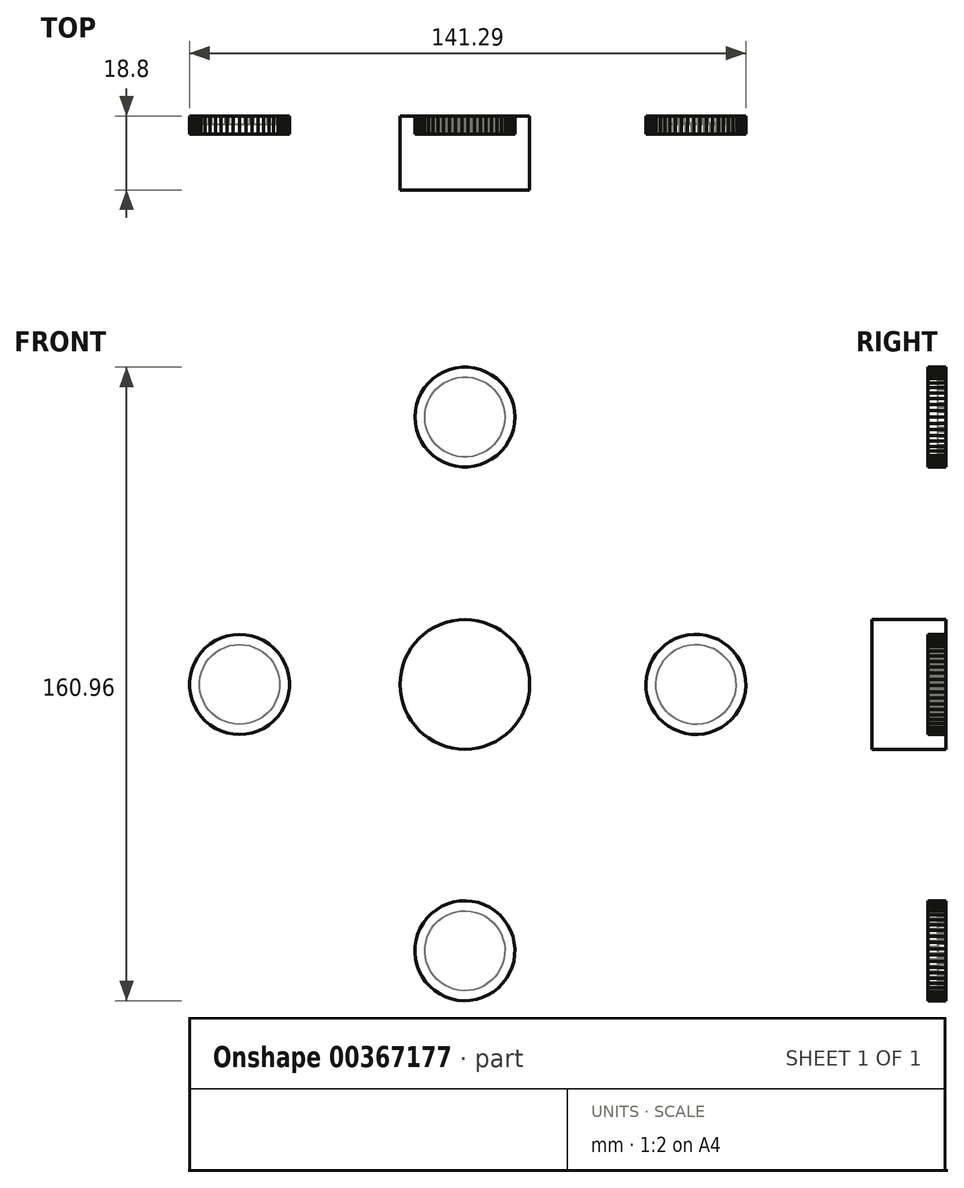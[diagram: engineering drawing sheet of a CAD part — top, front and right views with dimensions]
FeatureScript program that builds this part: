
annotation { "Feature Type Name" : "Feature", "Feature Type Description" : "" }
export const myFeature = defineFeature(function(context is Context, id is Id, definition is map)
    precondition{}
    {
        {
            var Q0;
            Q0=qCreatedBy(makeId("Front.planeOp"),FACE);
            var sketch = newSketch(context, id + "F0", { "sketchPlane" : qUnion([Q0])});
            skCircle(sketch, "E0", {"center": v(0, 0) * mm, "radius": 16.46 * mm});
            skSolve(sketch);
        }
        {
            var Q0;
            Q0=makeQuery(id+"F0.imprint","IMPRINT",FACE,{"disambiguationData":[TD([[makeQuery(id+"F0.imprint","IMPRINT",EDGE,{"derivedFrom":sQuery(id+"F0.wireOp",EDGE,"E0")}),1.0]])]});
            extrude(context, id + "F1", {"entities" : qUnion([Q0]), "depth" : 18.8 * mm});
        }
        {
            var Q0;
            Q0=qCreatedBy(makeId("Top.planeOp"),FACE);
            var sketch = newSketch(context, id + "F2", { "sketchPlane" : qUnion([Q0])});
            skCircle(sketch, "E1", {"center": v(0, -9.63) * mm, "radius": 6.4 * mm});
            skSolve(sketch);
        }
        {
            var Q0;
            Q0=sQuery(id+"F2.wireOp",EDGE,"E1");
            extrude(context, id + "F3", {"bodyType" : ToolBodyType.SURFACE, "surfaceEntities" : qUnion([Q0]), "endBound" : BoundingType.SYMMETRIC, "depth" : 134.62 * mm});
        }
        {
            var Q0;
            Q0=qCreatedBy(makeId("Right.planeOp"),FACE);
            var sketch = newSketch(context, id + "F4", { "sketchPlane" : qUnion([Q0])});
            skCircle(sketch, "E2", {"center": v(-9.55, 0) * mm, "radius": 4.67 * mm});
            skSolve(sketch);
        }
        {
            var Q0;
            Q0=sQuery(id+"F4.wireOp",EDGE,"E2");
            extrude(context, id + "F5", {"bodyType" : ToolBodyType.SURFACE, "surfaceEntities" : qUnion([Q0]), "endBound" : BoundingType.SYMMETRIC, "depth" : 115.82 * mm});
        }
        {
            var Q0;
            Q0=qCreatedBy(makeId("Front.planeOp"),FACE);
            var sketch = newSketch(context, id + "F6", { "sketchPlane" : qUnion([Q0])});
            skCircle(sketch, "E3.cCircle", {"center": v(0, 67.94) * mm, "radius": 12.67 * mm, "construction": true});
            skLineSegment(sketch, "E3.0", {"start": v(-0.8, 80.61) * mm, "end": v(0.8, 80.61) * mm});
            skLineSegment(sketch, "E3.1", {"start": v(0.8, 80.61) * mm, "end": v(2.38, 80.41) * mm});
            skLineSegment(sketch, "E3.2", {"start": v(2.38, 80.41) * mm, "end": v(3.92, 80.02) * mm});
            skLineSegment(sketch, "E3.3", {"start": v(3.92, 80.02) * mm, "end": v(5.4, 79.43) * mm});
            skLineSegment(sketch, "E3.4", {"start": v(5.4, 79.43) * mm, "end": v(6.8, 78.66) * mm});
            skLineSegment(sketch, "E3.5", {"start": v(6.8, 78.66) * mm, "end": v(8.1, 77.72) * mm});
            skLineSegment(sketch, "E3.6", {"start": v(8.1, 77.72) * mm, "end": v(9.26, 76.63) * mm});
            skLineSegment(sketch, "E3.7", {"start": v(9.26, 76.63) * mm, "end": v(10.27, 75.4) * mm});
            skLineSegment(sketch, "E3.8", {"start": v(10.27, 75.4) * mm, "end": v(11.13, 74.06) * mm});
            skLineSegment(sketch, "E3.9", {"start": v(11.13, 74.06) * mm, "end": v(11.8, 72.61) * mm});
            skLineSegment(sketch, "E3.10", {"start": v(11.8, 72.61) * mm, "end": v(12.3, 71.1) * mm});
            skLineSegment(sketch, "E3.11", {"start": v(12.3, 71.1) * mm, "end": v(12.6, 69.53) * mm});
            skLineSegment(sketch, "E3.12", {"start": v(12.6, 69.53) * mm, "end": v(12.7, 67.94) * mm});
            skLineSegment(sketch, "E3.13", {"start": v(12.7, 67.94) * mm, "end": v(12.6, 66.35) * mm});
            skLineSegment(sketch, "E3.14", {"start": v(12.6, 66.35) * mm, "end": v(12.3, 64.78) * mm});
            skLineSegment(sketch, "E3.15", {"start": v(12.3, 64.78) * mm, "end": v(11.8, 63.26) * mm});
            skLineSegment(sketch, "E3.16", {"start": v(11.8, 63.26) * mm, "end": v(11.13, 61.82) * mm});
            skLineSegment(sketch, "E3.17", {"start": v(11.13, 61.82) * mm, "end": v(10.27, 60.47) * mm});
            skLineSegment(sketch, "E3.18", {"start": v(10.27, 60.47) * mm, "end": v(9.26, 59.24) * mm});
            skLineSegment(sketch, "E3.19", {"start": v(9.26, 59.24) * mm, "end": v(8.1, 58.15) * mm});
            skLineSegment(sketch, "E3.20", {"start": v(8.1, 58.15) * mm, "end": v(6.8, 57.22) * mm});
            skLineSegment(sketch, "E3.21", {"start": v(6.8, 57.22) * mm, "end": v(5.4, 56.45) * mm});
            skLineSegment(sketch, "E3.22", {"start": v(5.4, 56.45) * mm, "end": v(3.92, 55.86) * mm});
            skLineSegment(sketch, "E3.23", {"start": v(3.92, 55.86) * mm, "end": v(2.38, 55.46) * mm});
            skLineSegment(sketch, "E3.24", {"start": v(2.38, 55.46) * mm, "end": v(0.8, 55.26) * mm});
            skLineSegment(sketch, "E3.25", {"start": v(0.8, 55.26) * mm, "end": v(-0.8, 55.26) * mm});
            skLineSegment(sketch, "E3.26", {"start": v(-0.8, 55.26) * mm, "end": v(-2.38, 55.46) * mm});
            skLineSegment(sketch, "E3.27", {"start": v(-2.38, 55.46) * mm, "end": v(-3.92, 55.86) * mm});
            skLineSegment(sketch, "E3.28", {"start": v(-3.92, 55.86) * mm, "end": v(-5.4, 56.45) * mm});
            skLineSegment(sketch, "E3.29", {"start": v(-5.4, 56.45) * mm, "end": v(-6.8, 57.22) * mm});
            skLineSegment(sketch, "E3.30", {"start": v(-6.8, 57.22) * mm, "end": v(-8.1, 58.15) * mm});
            skLineSegment(sketch, "E3.31", {"start": v(-8.1, 58.15) * mm, "end": v(-9.26, 59.24) * mm});
            skLineSegment(sketch, "E3.32", {"start": v(-9.26, 59.24) * mm, "end": v(-10.27, 60.47) * mm});
            skLineSegment(sketch, "E3.33", {"start": v(-10.27, 60.47) * mm, "end": v(-11.13, 61.82) * mm});
            skLineSegment(sketch, "E3.34", {"start": v(-11.13, 61.82) * mm, "end": v(-11.8, 63.26) * mm});
            skLineSegment(sketch, "E3.35", {"start": v(-11.8, 63.26) * mm, "end": v(-12.3, 64.78) * mm});
            skLineSegment(sketch, "E3.36", {"start": v(-12.3, 64.78) * mm, "end": v(-12.6, 66.35) * mm});
            skLineSegment(sketch, "E3.37", {"start": v(-12.6, 66.35) * mm, "end": v(-12.7, 67.94) * mm});
            skLineSegment(sketch, "E3.38", {"start": v(-12.7, 67.94) * mm, "end": v(-12.6, 69.53) * mm});
            skLineSegment(sketch, "E3.39", {"start": v(-12.6, 69.53) * mm, "end": v(-12.3, 71.1) * mm});
            skLineSegment(sketch, "E3.40", {"start": v(-12.3, 71.1) * mm, "end": v(-11.8, 72.61) * mm});
            skLineSegment(sketch, "E3.41", {"start": v(-11.8, 72.61) * mm, "end": v(-11.13, 74.06) * mm});
            skLineSegment(sketch, "E3.42", {"start": v(-11.13, 74.06) * mm, "end": v(-10.27, 75.4) * mm});
            skLineSegment(sketch, "E3.43", {"start": v(-10.27, 75.4) * mm, "end": v(-9.26, 76.63) * mm});
            skLineSegment(sketch, "E3.44", {"start": v(-9.26, 76.63) * mm, "end": v(-8.1, 77.72) * mm});
            skLineSegment(sketch, "E3.45", {"start": v(-8.1, 77.72) * mm, "end": v(-6.8, 78.66) * mm});
            skLineSegment(sketch, "E3.46", {"start": v(-6.8, 78.66) * mm, "end": v(-5.4, 79.43) * mm});
            skLineSegment(sketch, "E3.47", {"start": v(-5.4, 79.43) * mm, "end": v(-3.92, 80.02) * mm});
            skLineSegment(sketch, "E3.48", {"start": v(-3.92, 80.02) * mm, "end": v(-2.38, 80.41) * mm});
            skLineSegment(sketch, "E3.49", {"start": v(-2.38, 80.41) * mm, "end": v(-0.8, 80.61) * mm});
            skPoint(sketch, "E3.0.midPoint", {"position": v(0, 80.61) * mm});
            skCircle(sketch, "E4.cCircle", {"center": v(58.67, 0) * mm, "radius": 12.67 * mm, "construction": true});
            skLineSegment(sketch, "E4.0", {"start": v(46.98, 4.96) * mm, "end": v(47.7, 6.38) * mm});
            skLineSegment(sketch, "E4.1", {"start": v(47.7, 6.38) * mm, "end": v(48.58, 7.7) * mm});
            skLineSegment(sketch, "E4.2", {"start": v(48.58, 7.7) * mm, "end": v(49.63, 8.91) * mm});
            skLineSegment(sketch, "E4.3", {"start": v(49.63, 8.91) * mm, "end": v(50.81, 9.98) * mm});
            skLineSegment(sketch, "E4.4", {"start": v(50.81, 9.98) * mm, "end": v(52.13, 10.88) * mm});
            skLineSegment(sketch, "E4.5", {"start": v(52.13, 10.88) * mm, "end": v(53.54, 11.62) * mm});
            skLineSegment(sketch, "E4.6", {"start": v(53.54, 11.62) * mm, "end": v(55.04, 12.17) * mm});
            skLineSegment(sketch, "E4.7", {"start": v(55.04, 12.17) * mm, "end": v(56.6, 12.53) * mm});
            skLineSegment(sketch, "E4.8", {"start": v(56.6, 12.53) * mm, "end": v(58.18, 12.7) * mm});
            skLineSegment(sketch, "E4.9", {"start": v(58.18, 12.7) * mm, "end": v(59.77, 12.65) * mm});
            skLineSegment(sketch, "E4.10", {"start": v(59.77, 12.65) * mm, "end": v(61.35, 12.41) * mm});
            skLineSegment(sketch, "E4.11", {"start": v(61.35, 12.41) * mm, "end": v(62.89, 11.98) * mm});
            skLineSegment(sketch, "E4.12", {"start": v(62.89, 11.98) * mm, "end": v(64.35, 11.36) * mm});
            skLineSegment(sketch, "E4.13", {"start": v(64.35, 11.36) * mm, "end": v(65.73, 10.56) * mm});
            skLineSegment(sketch, "E4.14", {"start": v(65.73, 10.56) * mm, "end": v(67, 9.59) * mm});
            skLineSegment(sketch, "E4.15", {"start": v(67, 9.59) * mm, "end": v(68.14, 8.47) * mm});
            skLineSegment(sketch, "E4.16", {"start": v(68.14, 8.47) * mm, "end": v(69.12, 7.22) * mm});
            skLineSegment(sketch, "E4.17", {"start": v(69.12, 7.22) * mm, "end": v(69.95, 5.85) * mm});
            skLineSegment(sketch, "E4.18", {"start": v(69.95, 5.85) * mm, "end": v(70.6, 4.4) * mm});
            skLineSegment(sketch, "E4.19", {"start": v(70.6, 4.4) * mm, "end": v(71.05, 2.86) * mm});
            skLineSegment(sketch, "E4.20", {"start": v(71.05, 2.86) * mm, "end": v(71.3, 1.3) * mm});
            skLineSegment(sketch, "E4.21", {"start": v(71.3, 1.3) * mm, "end": v(71.37, -0.3) * mm});
            skLineSegment(sketch, "E4.22", {"start": v(71.37, -0.3) * mm, "end": v(71.23, -1.9) * mm});
            skLineSegment(sketch, "E4.23", {"start": v(71.23, -1.9) * mm, "end": v(70.9, -3.45) * mm});
            skLineSegment(sketch, "E4.24", {"start": v(70.9, -3.45) * mm, "end": v(70.37, -4.96) * mm});
            skLineSegment(sketch, "E4.25", {"start": v(70.37, -4.96) * mm, "end": v(69.65, -6.38) * mm});
            skLineSegment(sketch, "E4.26", {"start": v(69.65, -6.38) * mm, "end": v(68.77, -7.7) * mm});
            skLineSegment(sketch, "E4.27", {"start": v(68.77, -7.7) * mm, "end": v(67.72, -8.91) * mm});
            skLineSegment(sketch, "E4.28", {"start": v(67.72, -8.91) * mm, "end": v(66.53, -9.98) * mm});
            skLineSegment(sketch, "E4.29", {"start": v(66.53, -9.98) * mm, "end": v(65.22, -10.88) * mm});
            skLineSegment(sketch, "E4.30", {"start": v(65.22, -10.88) * mm, "end": v(63.8, -11.62) * mm});
            skLineSegment(sketch, "E4.31", {"start": v(63.8, -11.62) * mm, "end": v(62.3, -12.17) * mm});
            skLineSegment(sketch, "E4.32", {"start": v(62.3, -12.17) * mm, "end": v(60.76, -12.53) * mm});
            skLineSegment(sketch, "E4.33", {"start": v(60.76, -12.53) * mm, "end": v(59.17, -12.7) * mm});
            skLineSegment(sketch, "E4.34", {"start": v(59.17, -12.7) * mm, "end": v(57.57, -12.65) * mm});
            skLineSegment(sketch, "E4.35", {"start": v(57.57, -12.65) * mm, "end": v(56, -12.41) * mm});
            skLineSegment(sketch, "E4.36", {"start": v(56, -12.41) * mm, "end": v(54.46, -11.98) * mm});
            skLineSegment(sketch, "E4.37", {"start": v(54.46, -11.98) * mm, "end": v(53, -11.36) * mm});
            skLineSegment(sketch, "E4.38", {"start": v(53, -11.36) * mm, "end": v(51.62, -10.56) * mm});
            skLineSegment(sketch, "E4.39", {"start": v(51.62, -10.56) * mm, "end": v(50.35, -9.59) * mm});
            skLineSegment(sketch, "E4.40", {"start": v(50.35, -9.59) * mm, "end": v(49.21, -8.47) * mm});
            skLineSegment(sketch, "E4.41", {"start": v(49.21, -8.47) * mm, "end": v(48.22, -7.22) * mm});
            skLineSegment(sketch, "E4.42", {"start": v(48.22, -7.22) * mm, "end": v(47.4, -5.85) * mm});
            skLineSegment(sketch, "E4.43", {"start": v(47.4, -5.85) * mm, "end": v(46.76, -4.4) * mm});
            skLineSegment(sketch, "E4.44", {"start": v(46.76, -4.4) * mm, "end": v(46.3, -2.86) * mm});
            skLineSegment(sketch, "E4.45", {"start": v(46.3, -2.86) * mm, "end": v(46.04, -1.3) * mm});
            skLineSegment(sketch, "E4.46", {"start": v(46.04, -1.3) * mm, "end": v(45.98, 0.3) * mm});
            skLineSegment(sketch, "E4.47", {"start": v(45.98, 0.3) * mm, "end": v(46.12, 1.9) * mm});
            skLineSegment(sketch, "E4.48", {"start": v(46.12, 1.9) * mm, "end": v(46.45, 3.45) * mm});
            skLineSegment(sketch, "E4.49", {"start": v(46.45, 3.45) * mm, "end": v(46.98, 4.96) * mm});
            skPoint(sketch, "E4.0.midPoint", {"position": v(47.34, 5.67) * mm});
            skCircle(sketch, "E5.cCircle", {"center": v(-57.25, 0) * mm, "radius": 12.67 * mm, "construction": true});
            skLineSegment(sketch, "E5.0", {"start": v(-44.57, 0.8) * mm, "end": v(-44.57, -0.8) * mm});
            skLineSegment(sketch, "E5.1", {"start": v(-44.57, -0.8) * mm, "end": v(-44.77, -2.38) * mm});
            skLineSegment(sketch, "E5.2", {"start": v(-44.77, -2.38) * mm, "end": v(-45.17, -3.92) * mm});
            skLineSegment(sketch, "E5.3", {"start": v(-45.17, -3.92) * mm, "end": v(-45.76, -5.4) * mm});
            skLineSegment(sketch, "E5.4", {"start": v(-45.76, -5.4) * mm, "end": v(-46.53, -6.8) * mm});
            skLineSegment(sketch, "E5.5", {"start": v(-46.53, -6.8) * mm, "end": v(-47.46, -8.1) * mm});
            skLineSegment(sketch, "E5.6", {"start": v(-47.46, -8.1) * mm, "end": v(-48.56, -9.26) * mm});
            skLineSegment(sketch, "E5.7", {"start": v(-48.56, -9.26) * mm, "end": v(-49.78, -10.27) * mm});
            skLineSegment(sketch, "E5.8", {"start": v(-49.78, -10.27) * mm, "end": v(-51.13, -11.13) * mm});
            skLineSegment(sketch, "E5.9", {"start": v(-51.13, -11.13) * mm, "end": v(-52.57, -11.8) * mm});
            skLineSegment(sketch, "E5.10", {"start": v(-52.57, -11.8) * mm, "end": v(-54.1, -12.3) * mm});
            skLineSegment(sketch, "E5.11", {"start": v(-54.1, -12.3) * mm, "end": v(-55.66, -12.6) * mm});
            skLineSegment(sketch, "E5.12", {"start": v(-55.66, -12.6) * mm, "end": v(-57.25, -12.7) * mm});
            skLineSegment(sketch, "E5.13", {"start": v(-57.25, -12.7) * mm, "end": v(-58.84, -12.6) * mm});
            skLineSegment(sketch, "E5.14", {"start": v(-58.84, -12.6) * mm, "end": v(-60.4, -12.3) * mm});
            skLineSegment(sketch, "E5.15", {"start": v(-60.4, -12.3) * mm, "end": v(-61.92, -11.8) * mm});
            skLineSegment(sketch, "E5.16", {"start": v(-61.92, -11.8) * mm, "end": v(-63.37, -11.13) * mm});
            skLineSegment(sketch, "E5.17", {"start": v(-63.37, -11.13) * mm, "end": v(-64.71, -10.27) * mm});
            skLineSegment(sketch, "E5.18", {"start": v(-64.71, -10.27) * mm, "end": v(-65.94, -9.26) * mm});
            skLineSegment(sketch, "E5.19", {"start": v(-65.94, -9.26) * mm, "end": v(-67.03, -8.1) * mm});
            skLineSegment(sketch, "E5.20", {"start": v(-67.03, -8.1) * mm, "end": v(-67.97, -6.8) * mm});
            skLineSegment(sketch, "E5.21", {"start": v(-67.97, -6.8) * mm, "end": v(-68.74, -5.4) * mm});
            skLineSegment(sketch, "E5.22", {"start": v(-68.74, -5.4) * mm, "end": v(-69.33, -3.92) * mm});
            skLineSegment(sketch, "E5.23", {"start": v(-69.33, -3.92) * mm, "end": v(-69.72, -2.38) * mm});
            skLineSegment(sketch, "E5.24", {"start": v(-69.72, -2.38) * mm, "end": v(-69.92, -0.8) * mm});
            skLineSegment(sketch, "E5.25", {"start": v(-69.92, -0.8) * mm, "end": v(-69.92, 0.8) * mm});
            skLineSegment(sketch, "E5.26", {"start": v(-69.92, 0.8) * mm, "end": v(-69.72, 2.38) * mm});
            skLineSegment(sketch, "E5.27", {"start": v(-69.72, 2.38) * mm, "end": v(-69.33, 3.92) * mm});
            skLineSegment(sketch, "E5.28", {"start": v(-69.33, 3.92) * mm, "end": v(-68.74, 5.4) * mm});
            skLineSegment(sketch, "E5.29", {"start": v(-68.74, 5.4) * mm, "end": v(-67.97, 6.8) * mm});
            skLineSegment(sketch, "E5.30", {"start": v(-67.97, 6.8) * mm, "end": v(-67.03, 8.1) * mm});
            skLineSegment(sketch, "E5.31", {"start": v(-67.03, 8.1) * mm, "end": v(-65.94, 9.26) * mm});
            skLineSegment(sketch, "E5.32", {"start": v(-65.94, 9.26) * mm, "end": v(-64.71, 10.27) * mm});
            skLineSegment(sketch, "E5.33", {"start": v(-64.71, 10.27) * mm, "end": v(-63.37, 11.13) * mm});
            skLineSegment(sketch, "E5.34", {"start": v(-63.37, 11.13) * mm, "end": v(-61.92, 11.8) * mm});
            skLineSegment(sketch, "E5.35", {"start": v(-61.92, 11.8) * mm, "end": v(-60.4, 12.3) * mm});
            skLineSegment(sketch, "E5.36", {"start": v(-60.4, 12.3) * mm, "end": v(-58.84, 12.6) * mm});
            skLineSegment(sketch, "E5.37", {"start": v(-58.84, 12.6) * mm, "end": v(-57.25, 12.7) * mm});
            skLineSegment(sketch, "E5.38", {"start": v(-57.25, 12.7) * mm, "end": v(-55.66, 12.6) * mm});
            skLineSegment(sketch, "E5.39", {"start": v(-55.66, 12.6) * mm, "end": v(-54.1, 12.3) * mm});
            skLineSegment(sketch, "E5.40", {"start": v(-54.1, 12.3) * mm, "end": v(-52.57, 11.8) * mm});
            skLineSegment(sketch, "E5.41", {"start": v(-52.57, 11.8) * mm, "end": v(-51.13, 11.13) * mm});
            skLineSegment(sketch, "E5.42", {"start": v(-51.13, 11.13) * mm, "end": v(-49.78, 10.27) * mm});
            skLineSegment(sketch, "E5.43", {"start": v(-49.78, 10.27) * mm, "end": v(-48.56, 9.26) * mm});
            skLineSegment(sketch, "E5.44", {"start": v(-48.56, 9.26) * mm, "end": v(-47.46, 8.1) * mm});
            skLineSegment(sketch, "E5.45", {"start": v(-47.46, 8.1) * mm, "end": v(-46.53, 6.8) * mm});
            skLineSegment(sketch, "E5.46", {"start": v(-46.53, 6.8) * mm, "end": v(-45.76, 5.4) * mm});
            skLineSegment(sketch, "E5.47", {"start": v(-45.76, 5.4) * mm, "end": v(-45.17, 3.92) * mm});
            skLineSegment(sketch, "E5.48", {"start": v(-45.17, 3.92) * mm, "end": v(-44.77, 2.38) * mm});
            skLineSegment(sketch, "E5.49", {"start": v(-44.77, 2.38) * mm, "end": v(-44.57, 0.8) * mm});
            skPoint(sketch, "E5.0.midPoint", {"position": v(-44.57, 0) * mm});
            skCircle(sketch, "E6.cCircle", {"center": v(0, -67.66) * mm, "radius": 12.67 * mm, "construction": true});
            skLineSegment(sketch, "E6.0", {"start": v(-8.5, -58.21) * mm, "end": v(-7.24, -57.22) * mm});
            skLineSegment(sketch, "E6.1", {"start": v(-7.24, -57.22) * mm, "end": v(-5.88, -56.4) * mm});
            skLineSegment(sketch, "E6.2", {"start": v(-5.88, -56.4) * mm, "end": v(-4.42, -55.75) * mm});
            skLineSegment(sketch, "E6.3", {"start": v(-4.42, -55.75) * mm, "end": v(-2.9, -55.3) * mm});
            skLineSegment(sketch, "E6.4", {"start": v(-2.9, -55.3) * mm, "end": v(-1.32, -55.03) * mm});
            skLineSegment(sketch, "E6.5", {"start": v(-1.32, -55.03) * mm, "end": v(0.27, -54.96) * mm});
            skLineSegment(sketch, "E6.6", {"start": v(0.27, -54.96) * mm, "end": v(1.86, -55.1) * mm});
            skLineSegment(sketch, "E6.7", {"start": v(1.86, -55.1) * mm, "end": v(3.42, -55.43) * mm});
            skLineSegment(sketch, "E6.8", {"start": v(3.42, -55.43) * mm, "end": v(4.93, -55.95) * mm});
            skLineSegment(sketch, "E6.9", {"start": v(4.93, -55.95) * mm, "end": v(6.36, -56.66) * mm});
            skLineSegment(sketch, "E6.10", {"start": v(6.36, -56.66) * mm, "end": v(7.68, -57.55) * mm});
            skLineSegment(sketch, "E6.11", {"start": v(7.68, -57.55) * mm, "end": v(8.9, -58.59) * mm});
            skLineSegment(sketch, "E6.12", {"start": v(8.9, -58.59) * mm, "end": v(9.96, -59.77) * mm});
            skLineSegment(sketch, "E6.13", {"start": v(9.96, -59.77) * mm, "end": v(10.87, -61.08) * mm});
            skLineSegment(sketch, "E6.14", {"start": v(10.87, -61.08) * mm, "end": v(11.6, -62.5) * mm});
            skLineSegment(sketch, "E6.15", {"start": v(11.6, -62.5) * mm, "end": v(12.16, -64) * mm});
            skLineSegment(sketch, "E6.16", {"start": v(12.16, -64) * mm, "end": v(12.52, -65.55) * mm});
            skLineSegment(sketch, "E6.17", {"start": v(12.52, -65.55) * mm, "end": v(12.69, -67.13) * mm});
            skLineSegment(sketch, "E6.18", {"start": v(12.69, -67.13) * mm, "end": v(12.65, -68.73) * mm});
            skLineSegment(sketch, "E6.19", {"start": v(12.65, -68.73) * mm, "end": v(12.42, -70.3) * mm});
            skLineSegment(sketch, "E6.20", {"start": v(12.42, -70.3) * mm, "end": v(12, -71.84) * mm});
            skLineSegment(sketch, "E6.21", {"start": v(12, -71.84) * mm, "end": v(11.37, -73.31) * mm});
            skLineSegment(sketch, "E6.22", {"start": v(11.37, -73.31) * mm, "end": v(10.57, -74.7) * mm});
            skLineSegment(sketch, "E6.23", {"start": v(10.57, -74.7) * mm, "end": v(9.6, -75.96) * mm});
            skLineSegment(sketch, "E6.24", {"start": v(9.6, -75.96) * mm, "end": v(8.5, -77.1) * mm});
            skLineSegment(sketch, "E6.25", {"start": v(8.5, -77.1) * mm, "end": v(7.24, -78.1) * mm});
            skLineSegment(sketch, "E6.26", {"start": v(7.24, -78.1) * mm, "end": v(5.88, -78.92) * mm});
            skLineSegment(sketch, "E6.27", {"start": v(5.88, -78.92) * mm, "end": v(4.42, -79.56) * mm});
            skLineSegment(sketch, "E6.28", {"start": v(4.42, -79.56) * mm, "end": v(2.9, -80.02) * mm});
            skLineSegment(sketch, "E6.29", {"start": v(2.9, -80.02) * mm, "end": v(1.32, -80.29) * mm});
            skLineSegment(sketch, "E6.30", {"start": v(1.32, -80.29) * mm, "end": v(-0.27, -80.35) * mm});
            skLineSegment(sketch, "E6.31", {"start": v(-0.27, -80.35) * mm, "end": v(-1.86, -80.22) * mm});
            skLineSegment(sketch, "E6.32", {"start": v(-1.86, -80.22) * mm, "end": v(-3.42, -79.89) * mm});
            skLineSegment(sketch, "E6.33", {"start": v(-3.42, -79.89) * mm, "end": v(-4.93, -79.36) * mm});
            skLineSegment(sketch, "E6.34", {"start": v(-4.93, -79.36) * mm, "end": v(-6.36, -78.65) * mm});
            skLineSegment(sketch, "E6.35", {"start": v(-6.36, -78.65) * mm, "end": v(-7.68, -77.77) * mm});
            skLineSegment(sketch, "E6.36", {"start": v(-7.68, -77.77) * mm, "end": v(-8.9, -76.73) * mm});
            skLineSegment(sketch, "E6.37", {"start": v(-8.9, -76.73) * mm, "end": v(-9.96, -75.54) * mm});
            skLineSegment(sketch, "E6.38", {"start": v(-9.96, -75.54) * mm, "end": v(-10.87, -74.23) * mm});
            skLineSegment(sketch, "E6.39", {"start": v(-10.87, -74.23) * mm, "end": v(-11.6, -72.82) * mm});
            skLineSegment(sketch, "E6.40", {"start": v(-11.6, -72.82) * mm, "end": v(-12.16, -71.32) * mm});
            skLineSegment(sketch, "E6.41", {"start": v(-12.16, -71.32) * mm, "end": v(-12.52, -69.77) * mm});
            skLineSegment(sketch, "E6.42", {"start": v(-12.52, -69.77) * mm, "end": v(-12.69, -68.18) * mm});
            skLineSegment(sketch, "E6.43", {"start": v(-12.69, -68.18) * mm, "end": v(-12.65, -66.59) * mm});
            skLineSegment(sketch, "E6.44", {"start": v(-12.65, -66.59) * mm, "end": v(-12.42, -65.01) * mm});
            skLineSegment(sketch, "E6.45", {"start": v(-12.42, -65.01) * mm, "end": v(-12, -63.47) * mm});
            skLineSegment(sketch, "E6.46", {"start": v(-12, -63.47) * mm, "end": v(-11.37, -62) * mm});
            skLineSegment(sketch, "E6.47", {"start": v(-11.37, -62) * mm, "end": v(-10.57, -60.62) * mm});
            skLineSegment(sketch, "E6.48", {"start": v(-10.57, -60.62) * mm, "end": v(-9.6, -59.35) * mm});
            skLineSegment(sketch, "E6.49", {"start": v(-9.6, -59.35) * mm, "end": v(-8.5, -58.21) * mm});
            skPoint(sketch, "E6.0.midPoint", {"position": v(-7.87, -57.72) * mm});
            skSolve(sketch);
        }
        {
            var Q0;
            Q0=makeQuery(id+"F6.imprint","IMPRINT",FACE,{"disambiguationData":[TD([[makeQuery(id+"F6.imprint","IMPRINT",EDGE,{"derivedFrom":sQuery(id+"F6.wireOp",EDGE,"E6.0")}),-1.0]])]});
            var Q1;
            Q1=makeQuery(id+"F6.imprint","IMPRINT",FACE,{"disambiguationData":[TD([[makeQuery(id+"F6.imprint","IMPRINT",EDGE,{"derivedFrom":sQuery(id+"F6.wireOp",EDGE,"E4.0")}),-1.0]])]});
            var Q2;
            Q2=makeQuery(id+"F6.imprint","IMPRINT",FACE,{"disambiguationData":[TD([[makeQuery(id+"F6.imprint","IMPRINT",EDGE,{"derivedFrom":sQuery(id+"F6.wireOp",EDGE,"E3.0")}),-1.0]])]});
            var Q3;
            Q3=makeQuery(id+"F6.imprint","IMPRINT",FACE,{"disambiguationData":[TD([[makeQuery(id+"F6.imprint","IMPRINT",EDGE,{"derivedFrom":sQuery(id+"F6.wireOp",EDGE,"E5.0")}),-1.0]])]});
            extrude(context, id + "F7", {"entities" : qUnion([Q0, Q1, Q2, Q3]), "depth" : 4.57 * mm});
        }
        {
            var Q0;
            Q0=makeQuery(id+"F7.opExtrude","CAP_FACE",FACE,{"disambiguationData":[OSD([sQuery(id+"F6.wireOp",EDGE,"E4.0"),sQuery(id+"F6.wireOp",EDGE,"E4.1"),sQuery(id+"F6.wireOp",EDGE,"E4.2"),sQuery(id+"F6.wireOp",EDGE,"E4.3"),sQuery(id+"F6.wireOp",EDGE,"E4.4"),sQuery(id+"F6.wireOp",EDGE,"E4.5"),sQuery(id+"F6.wireOp",EDGE,"E4.6"),sQuery(id+"F6.wireOp",EDGE,"E4.7"),sQuery(id+"F6.wireOp",EDGE,"E4.8"),sQuery(id+"F6.wireOp",EDGE,"E4.9"),sQuery(id+"F6.wireOp",EDGE,"E4.10"),sQuery(id+"F6.wireOp",EDGE,"E4.11"),sQuery(id+"F6.wireOp",EDGE,"E4.12"),sQuery(id+"F6.wireOp",EDGE,"E4.13"),sQuery(id+"F6.wireOp",EDGE,"E4.14"),sQuery(id+"F6.wireOp",EDGE,"E4.15"),sQuery(id+"F6.wireOp",EDGE,"E4.16"),sQuery(id+"F6.wireOp",EDGE,"E4.17"),sQuery(id+"F6.wireOp",EDGE,"E4.18"),sQuery(id+"F6.wireOp",EDGE,"E4.19"),sQuery(id+"F6.wireOp",EDGE,"E4.20"),sQuery(id+"F6.wireOp",EDGE,"E4.21"),sQuery(id+"F6.wireOp",EDGE,"E4.22"),sQuery(id+"F6.wireOp",EDGE,"E4.23"),sQuery(id+"F6.wireOp",EDGE,"E4.24"),sQuery(id+"F6.wireOp",EDGE,"E4.25"),sQuery(id+"F6.wireOp",EDGE,"E4.26"),sQuery(id+"F6.wireOp",EDGE,"E4.27"),sQuery(id+"F6.wireOp",EDGE,"E4.28"),sQuery(id+"F6.wireOp",EDGE,"E4.29"),sQuery(id+"F6.wireOp",EDGE,"E4.30"),sQuery(id+"F6.wireOp",EDGE,"E4.31"),sQuery(id+"F6.wireOp",EDGE,"E4.32"),sQuery(id+"F6.wireOp",EDGE,"E4.33"),sQuery(id+"F6.wireOp",EDGE,"E4.34"),sQuery(id+"F6.wireOp",EDGE,"E4.35"),sQuery(id+"F6.wireOp",EDGE,"E4.36"),sQuery(id+"F6.wireOp",EDGE,"E4.37"),sQuery(id+"F6.wireOp",EDGE,"E4.38"),sQuery(id+"F6.wireOp",EDGE,"E4.39"),sQuery(id+"F6.wireOp",EDGE,"E4.40"),sQuery(id+"F6.wireOp",EDGE,"E4.41"),sQuery(id+"F6.wireOp",EDGE,"E4.42"),sQuery(id+"F6.wireOp",EDGE,"E4.43"),sQuery(id+"F6.wireOp",EDGE,"E4.44"),sQuery(id+"F6.wireOp",EDGE,"E4.45"),sQuery(id+"F6.wireOp",EDGE,"E4.46"),sQuery(id+"F6.wireOp",EDGE,"E4.47"),sQuery(id+"F6.wireOp",EDGE,"E4.48"),sQuery(id+"F6.wireOp",EDGE,"E4.49")])],"isStart":true});
            var Q1;
            Q1=makeQuery(id+"F7.opExtrude","CAP_FACE",FACE,{"disambiguationData":[OSD([sQuery(id+"F6.wireOp",EDGE,"E3.0"),sQuery(id+"F6.wireOp",EDGE,"E3.1"),sQuery(id+"F6.wireOp",EDGE,"E3.2"),sQuery(id+"F6.wireOp",EDGE,"E3.3"),sQuery(id+"F6.wireOp",EDGE,"E3.4"),sQuery(id+"F6.wireOp",EDGE,"E3.5"),sQuery(id+"F6.wireOp",EDGE,"E3.6"),sQuery(id+"F6.wireOp",EDGE,"E3.7"),sQuery(id+"F6.wireOp",EDGE,"E3.8"),sQuery(id+"F6.wireOp",EDGE,"E3.9"),sQuery(id+"F6.wireOp",EDGE,"E3.10"),sQuery(id+"F6.wireOp",EDGE,"E3.11"),sQuery(id+"F6.wireOp",EDGE,"E3.12"),sQuery(id+"F6.wireOp",EDGE,"E3.13"),sQuery(id+"F6.wireOp",EDGE,"E3.14"),sQuery(id+"F6.wireOp",EDGE,"E3.15"),sQuery(id+"F6.wireOp",EDGE,"E3.16"),sQuery(id+"F6.wireOp",EDGE,"E3.17"),sQuery(id+"F6.wireOp",EDGE,"E3.18"),sQuery(id+"F6.wireOp",EDGE,"E3.19"),sQuery(id+"F6.wireOp",EDGE,"E3.20"),sQuery(id+"F6.wireOp",EDGE,"E3.21"),sQuery(id+"F6.wireOp",EDGE,"E3.22"),sQuery(id+"F6.wireOp",EDGE,"E3.23"),sQuery(id+"F6.wireOp",EDGE,"E3.24"),sQuery(id+"F6.wireOp",EDGE,"E3.25"),sQuery(id+"F6.wireOp",EDGE,"E3.26"),sQuery(id+"F6.wireOp",EDGE,"E3.27"),sQuery(id+"F6.wireOp",EDGE,"E3.28"),sQuery(id+"F6.wireOp",EDGE,"E3.29"),sQuery(id+"F6.wireOp",EDGE,"E3.30"),sQuery(id+"F6.wireOp",EDGE,"E3.31"),sQuery(id+"F6.wireOp",EDGE,"E3.32"),sQuery(id+"F6.wireOp",EDGE,"E3.33"),sQuery(id+"F6.wireOp",EDGE,"E3.34"),sQuery(id+"F6.wireOp",EDGE,"E3.35"),sQuery(id+"F6.wireOp",EDGE,"E3.36"),sQuery(id+"F6.wireOp",EDGE,"E3.37"),sQuery(id+"F6.wireOp",EDGE,"E3.38"),sQuery(id+"F6.wireOp",EDGE,"E3.39"),sQuery(id+"F6.wireOp",EDGE,"E3.40"),sQuery(id+"F6.wireOp",EDGE,"E3.41"),sQuery(id+"F6.wireOp",EDGE,"E3.42"),sQuery(id+"F6.wireOp",EDGE,"E3.43"),sQuery(id+"F6.wireOp",EDGE,"E3.44"),sQuery(id+"F6.wireOp",EDGE,"E3.45"),sQuery(id+"F6.wireOp",EDGE,"E3.46"),sQuery(id+"F6.wireOp",EDGE,"E3.47"),sQuery(id+"F6.wireOp",EDGE,"E3.48"),sQuery(id+"F6.wireOp",EDGE,"E3.49")])],"isStart":true});
            var Q2;
            Q2=makeQuery(id+"F7.opExtrude","CAP_FACE",FACE,{"disambiguationData":[OSD([sQuery(id+"F6.wireOp",EDGE,"E6.0"),sQuery(id+"F6.wireOp",EDGE,"E6.1"),sQuery(id+"F6.wireOp",EDGE,"E6.2"),sQuery(id+"F6.wireOp",EDGE,"E6.3"),sQuery(id+"F6.wireOp",EDGE,"E6.4"),sQuery(id+"F6.wireOp",EDGE,"E6.5"),sQuery(id+"F6.wireOp",EDGE,"E6.6"),sQuery(id+"F6.wireOp",EDGE,"E6.7"),sQuery(id+"F6.wireOp",EDGE,"E6.8"),sQuery(id+"F6.wireOp",EDGE,"E6.9"),sQuery(id+"F6.wireOp",EDGE,"E6.10"),sQuery(id+"F6.wireOp",EDGE,"E6.11"),sQuery(id+"F6.wireOp",EDGE,"E6.12"),sQuery(id+"F6.wireOp",EDGE,"E6.13"),sQuery(id+"F6.wireOp",EDGE,"E6.14"),sQuery(id+"F6.wireOp",EDGE,"E6.15"),sQuery(id+"F6.wireOp",EDGE,"E6.16"),sQuery(id+"F6.wireOp",EDGE,"E6.17"),sQuery(id+"F6.wireOp",EDGE,"E6.18"),sQuery(id+"F6.wireOp",EDGE,"E6.19"),sQuery(id+"F6.wireOp",EDGE,"E6.20"),sQuery(id+"F6.wireOp",EDGE,"E6.21"),sQuery(id+"F6.wireOp",EDGE,"E6.22"),sQuery(id+"F6.wireOp",EDGE,"E6.23"),sQuery(id+"F6.wireOp",EDGE,"E6.24"),sQuery(id+"F6.wireOp",EDGE,"E6.25"),sQuery(id+"F6.wireOp",EDGE,"E6.26"),sQuery(id+"F6.wireOp",EDGE,"E6.27"),sQuery(id+"F6.wireOp",EDGE,"E6.28"),sQuery(id+"F6.wireOp",EDGE,"E6.29"),sQuery(id+"F6.wireOp",EDGE,"E6.30"),sQuery(id+"F6.wireOp",EDGE,"E6.31"),sQuery(id+"F6.wireOp",EDGE,"E6.32"),sQuery(id+"F6.wireOp",EDGE,"E6.33"),sQuery(id+"F6.wireOp",EDGE,"E6.34"),sQuery(id+"F6.wireOp",EDGE,"E6.35"),sQuery(id+"F6.wireOp",EDGE,"E6.36"),sQuery(id+"F6.wireOp",EDGE,"E6.37"),sQuery(id+"F6.wireOp",EDGE,"E6.38"),sQuery(id+"F6.wireOp",EDGE,"E6.39"),sQuery(id+"F6.wireOp",EDGE,"E6.40"),sQuery(id+"F6.wireOp",EDGE,"E6.41"),sQuery(id+"F6.wireOp",EDGE,"E6.42"),sQuery(id+"F6.wireOp",EDGE,"E6.43"),sQuery(id+"F6.wireOp",EDGE,"E6.44"),sQuery(id+"F6.wireOp",EDGE,"E6.45"),sQuery(id+"F6.wireOp",EDGE,"E6.46"),sQuery(id+"F6.wireOp",EDGE,"E6.47"),sQuery(id+"F6.wireOp",EDGE,"E6.48"),sQuery(id+"F6.wireOp",EDGE,"E6.49")])],"isStart":true});
            var Q3;
            Q3=makeQuery(id+"F7.opExtrude","CAP_FACE",FACE,{"disambiguationData":[OSD([sQuery(id+"F6.wireOp",EDGE,"E5.0"),sQuery(id+"F6.wireOp",EDGE,"E5.1"),sQuery(id+"F6.wireOp",EDGE,"E5.2"),sQuery(id+"F6.wireOp",EDGE,"E5.3"),sQuery(id+"F6.wireOp",EDGE,"E5.4"),sQuery(id+"F6.wireOp",EDGE,"E5.5"),sQuery(id+"F6.wireOp",EDGE,"E5.6"),sQuery(id+"F6.wireOp",EDGE,"E5.7"),sQuery(id+"F6.wireOp",EDGE,"E5.8"),sQuery(id+"F6.wireOp",EDGE,"E5.9"),sQuery(id+"F6.wireOp",EDGE,"E5.10"),sQuery(id+"F6.wireOp",EDGE,"E5.11"),sQuery(id+"F6.wireOp",EDGE,"E5.12"),sQuery(id+"F6.wireOp",EDGE,"E5.13"),sQuery(id+"F6.wireOp",EDGE,"E5.14"),sQuery(id+"F6.wireOp",EDGE,"E5.15"),sQuery(id+"F6.wireOp",EDGE,"E5.16"),sQuery(id+"F6.wireOp",EDGE,"E5.17"),sQuery(id+"F6.wireOp",EDGE,"E5.18"),sQuery(id+"F6.wireOp",EDGE,"E5.19"),sQuery(id+"F6.wireOp",EDGE,"E5.20"),sQuery(id+"F6.wireOp",EDGE,"E5.21"),sQuery(id+"F6.wireOp",EDGE,"E5.22"),sQuery(id+"F6.wireOp",EDGE,"E5.23"),sQuery(id+"F6.wireOp",EDGE,"E5.24"),sQuery(id+"F6.wireOp",EDGE,"E5.25"),sQuery(id+"F6.wireOp",EDGE,"E5.26"),sQuery(id+"F6.wireOp",EDGE,"E5.27"),sQuery(id+"F6.wireOp",EDGE,"E5.28"),sQuery(id+"F6.wireOp",EDGE,"E5.29"),sQuery(id+"F6.wireOp",EDGE,"E5.30"),sQuery(id+"F6.wireOp",EDGE,"E5.31"),sQuery(id+"F6.wireOp",EDGE,"E5.32"),sQuery(id+"F6.wireOp",EDGE,"E5.33"),sQuery(id+"F6.wireOp",EDGE,"E5.34"),sQuery(id+"F6.wireOp",EDGE,"E5.35"),sQuery(id+"F6.wireOp",EDGE,"E5.36"),sQuery(id+"F6.wireOp",EDGE,"E5.37"),sQuery(id+"F6.wireOp",EDGE,"E5.38"),sQuery(id+"F6.wireOp",EDGE,"E5.39"),sQuery(id+"F6.wireOp",EDGE,"E5.40"),sQuery(id+"F6.wireOp",EDGE,"E5.41"),sQuery(id+"F6.wireOp",EDGE,"E5.42"),sQuery(id+"F6.wireOp",EDGE,"E5.43"),sQuery(id+"F6.wireOp",EDGE,"E5.44"),sQuery(id+"F6.wireOp",EDGE,"E5.45"),sQuery(id+"F6.wireOp",EDGE,"E5.46"),sQuery(id+"F6.wireOp",EDGE,"E5.47"),sQuery(id+"F6.wireOp",EDGE,"E5.48"),sQuery(id+"F6.wireOp",EDGE,"E5.49")])],"isStart":true});
            shell(context, id + "F8", {"entities" : qUnion([Q0, Q1, Q2, Q3]), "thickness" : 2.54 * mm});
        }
    });
